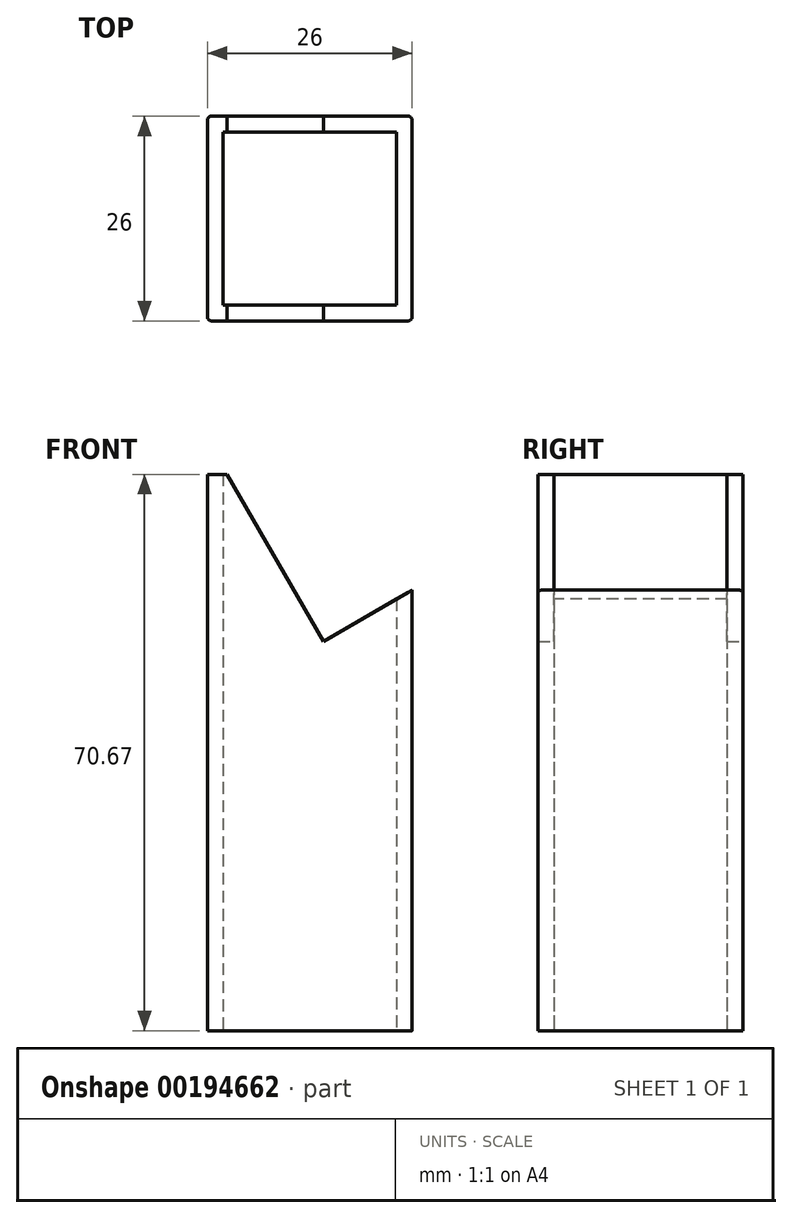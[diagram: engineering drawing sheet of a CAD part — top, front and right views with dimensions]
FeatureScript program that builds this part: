
annotation { "Feature Type Name" : "Feature", "Feature Type Description" : "" }
export const myFeature = defineFeature(function(context is Context, id is Id, definition is map)
    precondition{}
    {
        {
            var Q0;
            Q0=qCreatedBy(makeId("Top.planeOp"),FACE);
            var sketch = newSketch(context, id + "F0", { "sketchPlane" : qUnion([Q0])});
            skLineSegment(sketch, "E0.bottom", {"start": v(-13, -13) * mm, "end": v(13, -13) * mm});
            skLineSegment(sketch, "E0.top", {"start": v(-13, 13) * mm, "end": v(13, 13) * mm});
            skLineSegment(sketch, "E0.left", {"start": v(-13, 13) * mm, "end": v(-13, -13) * mm});
            skLineSegment(sketch, "E0.right", {"start": v(13, 13) * mm, "end": v(13, -13) * mm});
            skLineSegment(sketch, "E1.0", {"start": v(-11, 11) * mm, "end": v(11, 11) * mm});
            skLineSegment(sketch, "E1.1", {"start": v(-11, 11) * mm, "end": v(-11, -11) * mm});
            skLineSegment(sketch, "E1.2", {"start": v(-11, -11) * mm, "end": v(11, -11) * mm});
            skLineSegment(sketch, "E1.3", {"start": v(11, 11) * mm, "end": v(11, -11) * mm});
            skSolve(sketch);
        }
        {
            var Q0;
            Q0=makeQuery(id+"F0.imprint","IMPRINT",FACE,{"disambiguationData":[TD([[makeQuery(id+"F0.imprint","IMPRINT",EDGE,{"derivedFrom":sQuery(id+"F0.wireOp",EDGE,"E0.bottom")}),1.0]])]});
            extrude(context, id + "F1", {"entities" : qUnion([Q0]), "depth" : 75 * mm});
        }
        {
            var Q0;
            Q0=makeQuery(id+"F1.opExtrude","SWEPT_FACE",FACE,{"disambiguationData":[OSD([sQuery(id+"F0.wireOp",EDGE,"E0.top")])]});
            var sketch = newSketch(context, id + "F2", { "sketchPlane" : qUnion([Q0])});
            skLineSegment(sketch, "E2", {"start": v(-1.74, 49.47) * mm, "end": v(10.5, 70.67) * mm});
            skLineSegment(sketch, "E3", {"start": v(13, 75) * mm, "end": v(-8.74, 75) * mm});
            skLineSegment(sketch, "E4", {"start": v(-1.74, 49.47) * mm, "end": v(-13, 55.97) * mm});
            skLineSegment(sketch, "E5", {"start": v(-13, 55.97) * mm, "end": v(-13, 75) * mm});
            skLineSegment(sketch, "E6", {"start": v(-13, 75) * mm, "end": v(13, 75) * mm});
            skLineSegment(sketch, "E7", {"start": v(10.5, 70.67) * mm, "end": v(13, 70.67) * mm});
            skLineSegment(sketch, "E8", {"start": v(13, 70.67) * mm, "end": v(13, 75) * mm});
            skSolve(sketch);
        }
        {
            var Q0;
            Q0=makeQuery(id+"F2.imprint","IMPRINT",FACE,{"disambiguationData":[TD([[makeQuery(id+"F2.imprint","IMPRINT",EDGE,{"derivedFrom":sQuery(id+"F2.wireOp",EDGE,"5Q2Xg9YF-kZfs-iRod-i2Ed-5O1OxSXWWwP6")}),1.0]])]});
            var Q1;
            {var subQ0=sQuery(id+"F2.wireOp",EDGE,"E2");Q1=makeQuery(id+"F2.imprint","IMPRINT",FACE,{"disambiguationData":[TD([[makeQuery(id+"F2.imprint","IMPRINT",EDGE,{"derivedFrom":subQ0}),1.0]])]});}
            extrude(context, id + "F3", {"entities" : qUnion([Q0, Q1]), "operationType" : NewBodyOperationType.REMOVE, "endBound" : BoundingType.THROUGH_ALL, "oppositeDirection" : true, "depth" : 25.4 * mm});
        }
        {
            var Q0;
            Q0=makeQuery(id+"F1.opExtrude","SWEPT_EDGE",EDGE,{"disambiguationData":[OSD([sQuery(id+"F0.wireOp",EDGE,"E0.top"),sQuery(id+"F0.wireOp",EDGE,"E0.right")])]});
            var Q1;
            Q1=makeQuery(id+"F1.opExtrude","SWEPT_EDGE",EDGE,{"disambiguationData":[OSD([sQuery(id+"F0.wireOp",EDGE,"E0.top"),sQuery(id+"F0.wireOp",EDGE,"E0.left")])]});
            var Q2;
            Q2=makeQuery(id+"F1.opExtrude","SWEPT_EDGE",EDGE,{"disambiguationData":[OSD([sQuery(id+"F0.wireOp",EDGE,"E0.bottom"),sQuery(id+"F0.wireOp",EDGE,"E0.left")])]});
            var Q3;
            Q3=makeQuery(id+"F1.opExtrude","SWEPT_EDGE",EDGE,{"disambiguationData":[OSD([sQuery(id+"F0.wireOp",EDGE,"E0.bottom"),sQuery(id+"F0.wireOp",EDGE,"E0.right")])]});
            fillet(context, id + "F4", {"entities" : qUnion([Q0, Q1, Q2, Q3]), "radius" : 0.5 * mm, "tangentPropagation" : true, "allowEdgeOverflow" : false});
        }
    });
